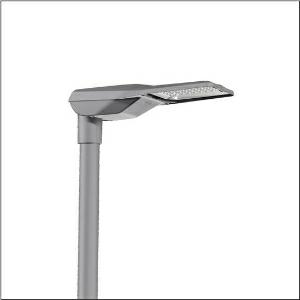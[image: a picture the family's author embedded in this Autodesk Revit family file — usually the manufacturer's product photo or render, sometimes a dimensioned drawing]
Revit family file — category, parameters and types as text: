
# Revit family: streetlight_sl_21_iq_mini___stw1_0a_5xe2e41d08hb_667c
name_source: partatom
category: Lighting Fixtures
units: mm (PartAtom-declared; Revit-internal decimal feet)

## family parameters
Cut with Voids When Loaded = No
Host = Face
Light Source = No
Part Type = Normal
Room Calculation Point = No
Round Connector Dimension = Use Diameter
Shared = No

## types (1)
- --- (1 x LED, 9860 lm, 70.9 W, 4000K)
    Apparent Load = 71 VA
    CIE Flux Codes = 38 75 98 100 100
    Color Rendering = 70
    Color Temperature = 4000K
    Default Elevation = 1800 mm
    Description = Streetlight SL 21 iQ mini, mast luminaire, primary light control with lens, of PMMA, primary optical cover: cover, of toughened safety glass, transparent, light distribution: STW1.0a, light emission: direct distribution, primary light characteristic: asymmetric, installation type: post-top, side-entry, LED, High Power LED, rated luminous flux: 9.860lm, luminous efficacy: 139lm/W, light colour: 740, colour temperature: 4000K, control gear: iQ-Comfort, control: Auto-Match, Temp-Guard, Lumen-Switch, Night-Set, Smart-Wire, Light-Fading, Desk-Remote (wireless, voltage-free reading and setting of iQ features in the workshop via application-optimized NFC function/RFID function), optimised constant luminous flux control (CLO 2.0), pre-setting: linear dimming characteristic, mains connection: 220..240V, AC, 50/60Hz, start of lifetime: 71W, end of service life: 75W, reduction: 31W, luminaire housing, of diecast aluminium, powder-coated, Siteco® metallic grey (DB 702S), corrosivity category C5 mid according to DIN EN ISO 12944, please order mast flange separately, inclination adjustable: 0°, 5°, 10°, 15°, sealing non-destructively replaceable, multi-level sealing system, length: 628mm, width: 235mm, height: 110mm, mast flange for spigot size: 42mm (side-entry): 5XC10008XM4, 60/48mm (side-entry/post-top): 5XC10108XM2, 76/60mm (side-entry/post-top): 5XC10108XM1, mounting height: 4..8m, protection rating (complete): IP66, insulation class (complete): insulation class II (safety insulation), certification: CE, ENEC, ENEC+, VDE, impact resistance: IK10, permissible operating ambient temperature for outdoor applications: -40..+50°C, standard-compliant lighting for roads and squares, packaging unit: 1 piece

Light Distribution: STW1.0a
    Height = 110 mm
    Lamp = 1 x LED
    Lamp Light Flux = 9860 lm
    Lamp Power = 70.9 W
    Lamp count = 1
    Length = 625 mm
    Luminous efficacy = 139 lm/W
    Manufacturer = Siteco
    ModVariant = No
    Model = 5XE2E41D08HB
    Number of Poles = 1
    OnlyDefault = Yes
    Power Factor = 1
    Product Name = Streetlight SL 21 iQ mini | STW1.0a
    Product group = mast luminaire | pylon top
    ProductGroupID = 6100
    Protection Class = Protection class II
    Protection Degree = IP 66
    RLX_Detail_Level = 1
    RLX_Emergency_Light_Flux = 0 lm
    RLX_Emergency_Type = 0
    RLX_Emergency_Type_DB = No
    RlxData = <blob elided: 26345 chars, md5=6223c8d7>
    Socket = socket
    Standby Power = 0 W
    System Light Flux = 9860 lm
    System Power = 71 W
    Type Comments = factory setting: luminous flux: 100 % | dim-lin: 254 | 711 mA
    Type Image = l_1003519.jpg
    URL = http://relux.com
    VarID = @adj_179249
    Voltage = 0 V
    Weight = 0.00 kg
    Width = 234 mm

## geometry (parser evidence)
native form markers: Blend x4, Sweep x11
no freeform markers — native parametric forms only
